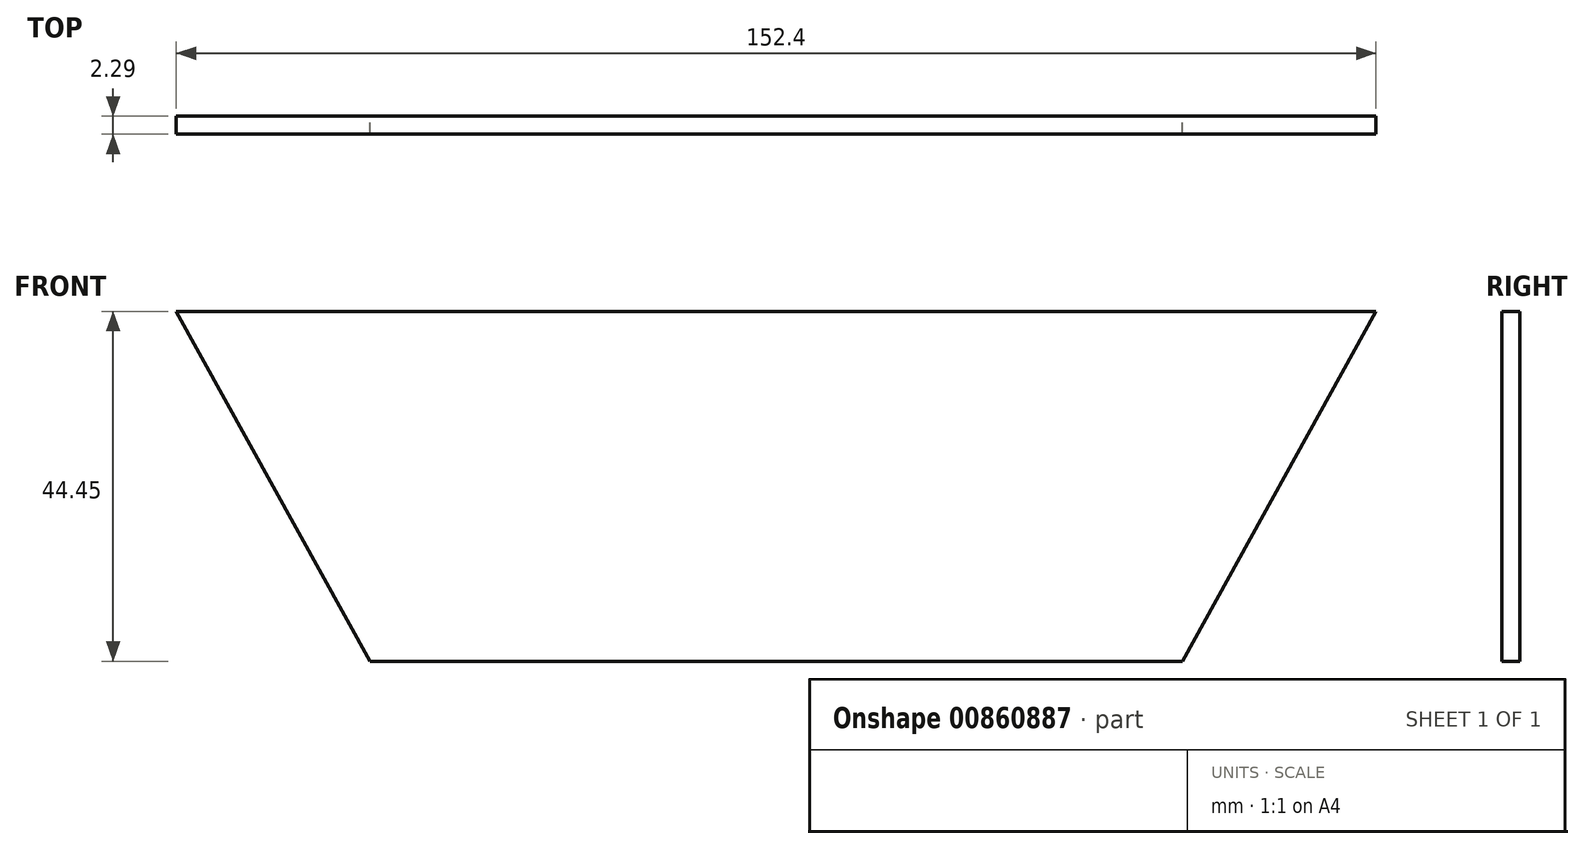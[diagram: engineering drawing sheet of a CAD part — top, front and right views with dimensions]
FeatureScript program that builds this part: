
annotation { "Feature Type Name" : "Feature", "Feature Type Description" : "" }
export const myFeature = defineFeature(function(context is Context, id is Id, definition is map)
    precondition{}
    {
        {
            var Q0;
            Q0=qCreatedBy(makeId("Front.planeOp"),FACE);
            var sketch = newSketch(context, id + "F0", { "sketchPlane" : qUnion([Q0])});
            skLineSegment(sketch, "E0", {"start": v(51.6, -1.63) * mm, "end": v(76.2, 42.82) * mm});
            skLineSegment(sketch, "E1", {"start": v(76.2, 42.82) * mm, "end": v(0, 42.82) * mm});
            skLineSegment(sketch, "E2.MirrorCS", {"start": v(-76.2, 42.82) * mm, "end": v(0, 42.82) * mm});
            skLineSegment(sketch, "E3.MirrorCS", {"start": v(-51.6, -1.63) * mm, "end": v(-76.2, 42.82) * mm});
            skLineSegment(sketch, "E4", {"start": v(-51.6, -1.63) * mm, "end": v(51.6, -1.63) * mm});
            skSolve(sketch);
        }
        {
            var Q0;
            Q0 = qSketchRegion(id + "F0", true);
            extrude(context, id + "F1", {"entities" : qUnion([Q0]), "depth" : 2.3 * mm, "offsetDistance" : 25.4 * mm});
        }
    });
